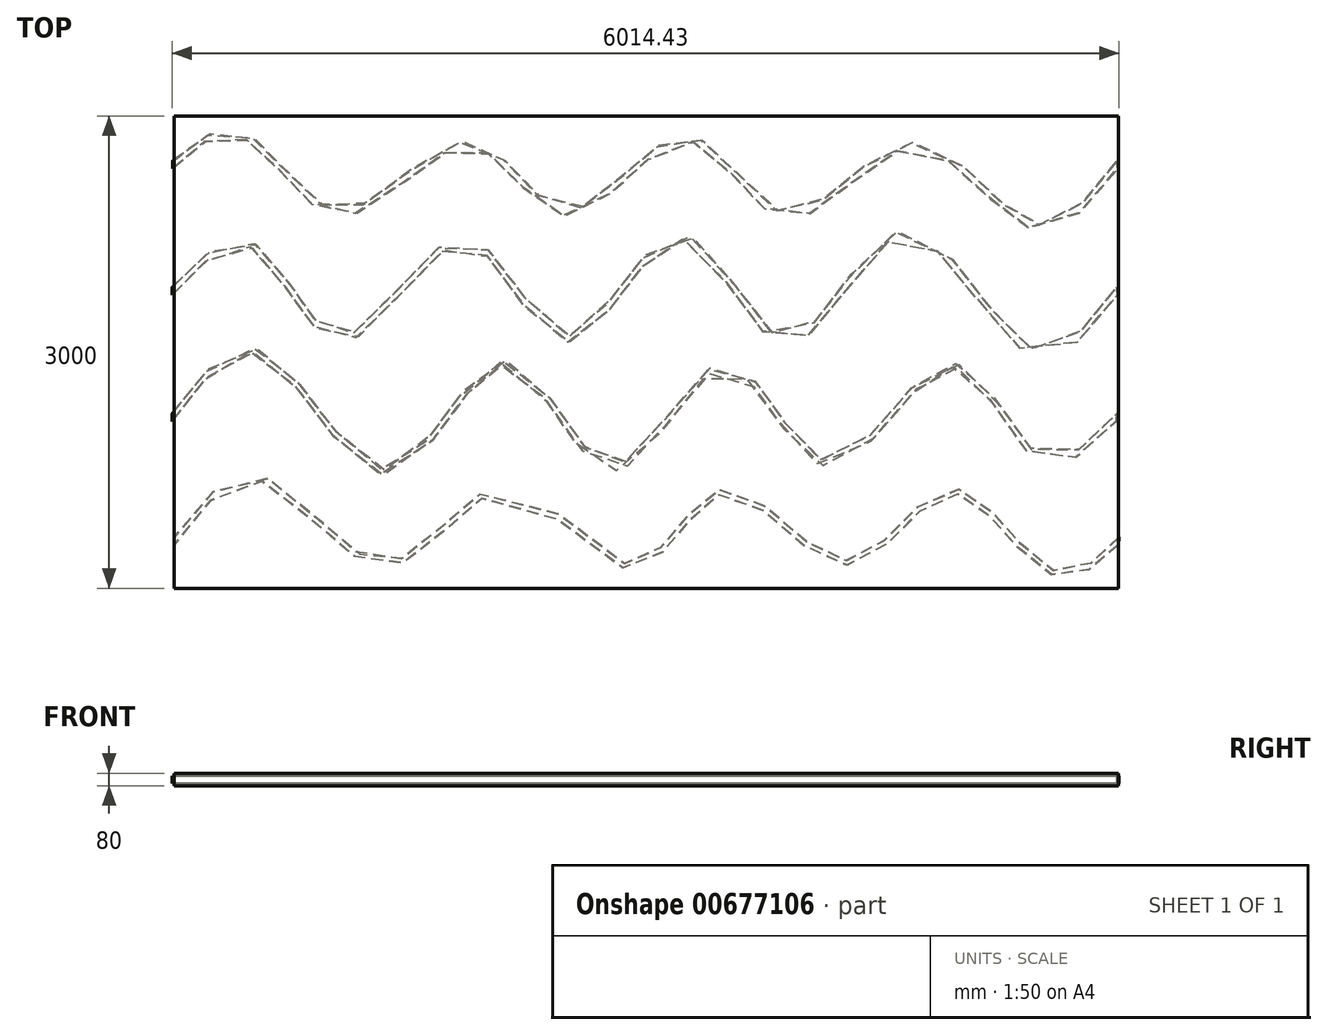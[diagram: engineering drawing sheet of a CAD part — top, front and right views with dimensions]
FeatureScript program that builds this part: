
annotation { "Feature Type Name" : "Feature", "Feature Type Description" : "" }
export const myFeature = defineFeature(function(context is Context, id is Id, definition is map)
    precondition{}
    {
        {
            var Q0;
            Q0=qCreatedBy(makeId("Top.planeOp"),FACE);
            var sketch = newSketch(context, id + "F0", { "sketchPlane" : qUnion([Q0])});
            skLineSegment(sketch, "E0", {"start": v(-2991.88, -1500) * mm, "end": v(-2991.88, 1500) * mm});
            skLineSegment(sketch, "E1", {"start": v(3008.12, -1500) * mm, "end": v(3008.12, 1500) * mm});
            skLineSegment(sketch, "E2", {"start": v(-2991.88, -1200) * mm, "end": v(3008.12, -1200) * mm, "construction": true});
            skLineSegment(sketch, "E3", {"start": v(3008.12, -400) * mm, "end": v(-2991.88, -400) * mm, "construction": true});
            skLineSegment(sketch, "E4", {"start": v(3008.12, 400) * mm, "end": v(-2991.88, 400) * mm, "construction": true});
            skLineSegment(sketch, "E5", {"start": v(-2991.88, 1200) * mm, "end": v(3008.12, 1200) * mm, "construction": true});
            skPoint(sketch, "E6", {"position": v(-2991.88, 0) * mm});
            skLineSegment(sketch, "E7", {"start": v(-2991.88, 0) * mm, "end": v(3008.12, 0) * mm, "construction": true});
            skFitSpline(sketch, "E8", {"points": [v(-2991.88, -1200) * mm, v(-2427.8, -807.78) * mm, v(-1636.22, -1350.54) * mm, v(-882.34, -866.9) * mm, v(-73.82, -1362.42) * mm, v(511.1, -883.78) * mm, v(1280.65, -1338.66) * mm, v(1938.3, -883.78) * mm, v(2546.02, -1380.24) * mm, v(3008.12, -1200) * mm], "startDerivative": vector(5576.14, 7459) * mm, "endDerivative": vector(5802.3, 6106.95) * mm});
            skFitSpline(sketch, "E9", {"points": [v(-2991.88, -400) * mm, v(-2427.8, -7.78) * mm, v(-1625.51, -759.39) * mm, v(-882.34, -66.9) * mm, v(-206.74, -734.05) * mm, v(511.1, -83.78) * mm, v(1161.36, -708.72) * mm, v(1938.3, -83.78) * mm, v(2504.13, -674.94) * mm, v(3008.12, -400) * mm], "startDerivative": vector(5576.14, 7459) * mm, "endDerivative": vector(5802.3, 6106.95) * mm});
            skFitSpline(sketch, "E10", {"points": [v(3008.12, 400) * mm, v(2444.03, 7.78) * mm, v(1641.75, 759.39) * mm, v(898.58, 66.9) * mm, v(222.97, 734.05) * mm, v(-494.86, 83.78) * mm, v(-1145.13, 708.72) * mm, v(-1922.07, 83.78) * mm, v(-2487.9, 674.94) * mm, v(-2991.88, 400) * mm], "startDerivative": vector(-5576.14, -7459) * mm, "endDerivative": vector(-5802.3, -6106.95) * mm});
            skFitSpline(sketch, "E11", {"points": [v(3008.12, 1200) * mm, v(2444.03, 807.78) * mm, v(1702.44, 1316.83) * mm, v(898.58, 866.9) * mm, v(264.8, 1358.41) * mm, v(-494.86, 883.78) * mm, v(-1107.5, 1322.77) * mm, v(-1922.07, 883.78) * mm, v(-2497.62, 1346.53) * mm, v(-2991.88, 1200) * mm], "startDerivative": vector(-5576.14, -7459) * mm, "endDerivative": vector(-5802.3, -6106.95) * mm});
            skLineSegment(sketch, "E12", {"start": v(-2991.88, 1500) * mm, "end": v(3008.12, 1500) * mm});
            skLineSegment(sketch, "E13", {"start": v(3008.12, -1500) * mm, "end": v(-2991.88, -1500) * mm});
            skSolve(sketch);
        }
        {
            var Q0;
            {var subQ0=sQuery(id+"F0.wireOp",EDGE,"E9");Q0=makeQuery(id+"F0.imprint","IMPRINT",FACE,{"disambiguationData":[TD([[makeQuery(id+"F0.imprint","IMPRINT",EDGE,{"derivedFrom":subQ0}),1.0]])]});}
            var Q1;
            {var subQ2=sQuery(id+"F0.wireOp",EDGE,"E11");Q1=makeQuery(id+"F0.imprint","IMPRINT",FACE,{"disambiguationData":[TD([[makeQuery(id+"F0.imprint","IMPRINT",EDGE,{"derivedFrom":subQ2}),-1.0]])]});}
            var Q2;
            {var subQ0=sQuery(id+"F0.wireOp",EDGE,"E8");Q2=makeQuery(id+"F0.imprint","IMPRINT",FACE,{"disambiguationData":[TD([[makeQuery(id+"F0.imprint","IMPRINT",EDGE,{"derivedFrom":subQ0}),1.0]])]});}
            var Q3;
            {var subQ2=sQuery(id+"F0.wireOp",EDGE,"E8");Q3=makeQuery(id+"F0.imprint","IMPRINT",FACE,{"disambiguationData":[TD([[makeQuery(id+"F0.imprint","IMPRINT",EDGE,{"derivedFrom":subQ2}),-1.0]])]});}
            var Q4;
            {var subQ0=sQuery(id+"F0.wireOp",EDGE,"E10");Q4=makeQuery(id+"F0.imprint","IMPRINT",FACE,{"disambiguationData":[TD([[makeQuery(id+"F0.imprint","IMPRINT",EDGE,{"derivedFrom":subQ0}),-1.0]])]});}
            extrude(context, id + "F1", {"entities" : qUnion([Q0, Q1, Q2, Q3, Q4]), "depth" : 80 * mm, "offsetDistance" : 25 * mm, "symmetric" : true});
        }
        {
            var Q0;
            Q0=makeQuery(id+"F1.opExtrude","SWEPT_FACE",FACE,{"disambiguationData":[OSD([sQuery(id+"F0.wireOp",EDGE,"E0")])]});
            var sketch = newSketch(context, id + "F2", { "sketchPlane" : qUnion([Q0])});
            skLineSegment(sketch, "E14.bottom", {"start": v(1485, -27) * mm, "end": v(-1485, -27) * mm});
            skLineSegment(sketch, "E14.top", {"start": v(1485, 27) * mm, "end": v(-1485, 27) * mm});
            skLineSegment(sketch, "E14.left", {"start": v(1485, -27) * mm, "end": v(1485, 27) * mm});
            skLineSegment(sketch, "E14.right", {"start": v(-1485, -27) * mm, "end": v(-1485, 27) * mm});
            skPoint(sketch, "E14.middle", {"position": v(0, 0) * mm});
            skCircle(sketch, "E15", {"center": v(-1200, 0) * mm, "radius": 25 * mm});
            skCircle(sketch, "E16", {"center": v(-400, 0) * mm, "radius": 25 * mm});
            skCircle(sketch, "E17", {"center": v(400, 0) * mm, "radius": 25 * mm});
            skCircle(sketch, "E18", {"center": v(1200, 0) * mm, "radius": 25 * mm});
            skCircle(sketch, "E19.0", {"center": v(-1200, 0) * mm, "radius": 20 * mm});
            skCircle(sketch, "E20.0", {"center": v(-400, 0) * mm, "radius": 23 * mm});
            skCircle(sketch, "E21.0", {"center": v(400, 0) * mm, "radius": 23 * mm});
            skCircle(sketch, "E22.0", {"center": v(1200, 0) * mm, "radius": 23 * mm});
            skSolve(sketch);
        }
        {
            var Q0;
            Q0=makeQuery(id+"F2.imprint","IMPRINT",FACE,{"disambiguationData":[TD([[makeQuery(id+"F2.imprint","IMPRINT",EDGE,{"derivedFrom":sQuery(id+"F2.wireOp",EDGE,"E15")}),1.0]])]});
            var Q1;
            Q1=sQuery(id+"F0.wireOp",EDGE,"E11");
            sweep(context, id + "F3", {"profiles" : qUnion([Q0]), "path" : qUnion([Q1])});
        }
        {
            var Q0;
            Q0=makeQuery(id+"F2.imprint","IMPRINT",FACE,{"disambiguationData":[TD([[makeQuery(id+"F2.imprint","IMPRINT",EDGE,{"derivedFrom":sQuery(id+"F2.wireOp",EDGE,"E16")}),1.0]])]});
            var Q1;
            Q1=sQuery(id+"F0.wireOp",EDGE,"E10");
            sweep(context, id + "F4", {"profiles" : qUnion([Q0]), "path" : qUnion([Q1])});
        }
        {
            var Q0;
            Q0=makeQuery(id+"F2.imprint","IMPRINT",FACE,{"disambiguationData":[TD([[makeQuery(id+"F2.imprint","IMPRINT",EDGE,{"derivedFrom":sQuery(id+"F2.wireOp",EDGE,"E17")}),1.0]])]});
            var Q1;
            Q1=sQuery(id+"F0.wireOp",EDGE,"E9");
            sweep(context, id + "F5", {"profiles" : qUnion([Q0]), "path" : qUnion([Q1])});
        }
        {
            var Q0;
            Q0=makeQuery(id+"F2.imprint","IMPRINT",FACE,{"disambiguationData":[TD([[makeQuery(id+"F2.imprint","IMPRINT",EDGE,{"derivedFrom":sQuery(id+"F2.wireOp",EDGE,"E18")}),1.0]])]});
            var Q1;
            Q1=sQuery(id+"F0.wireOp",EDGE,"E8");
            sweep(context, id + "F6", {"profiles" : qUnion([Q0]), "path" : qUnion([Q1])});
        }
    });
